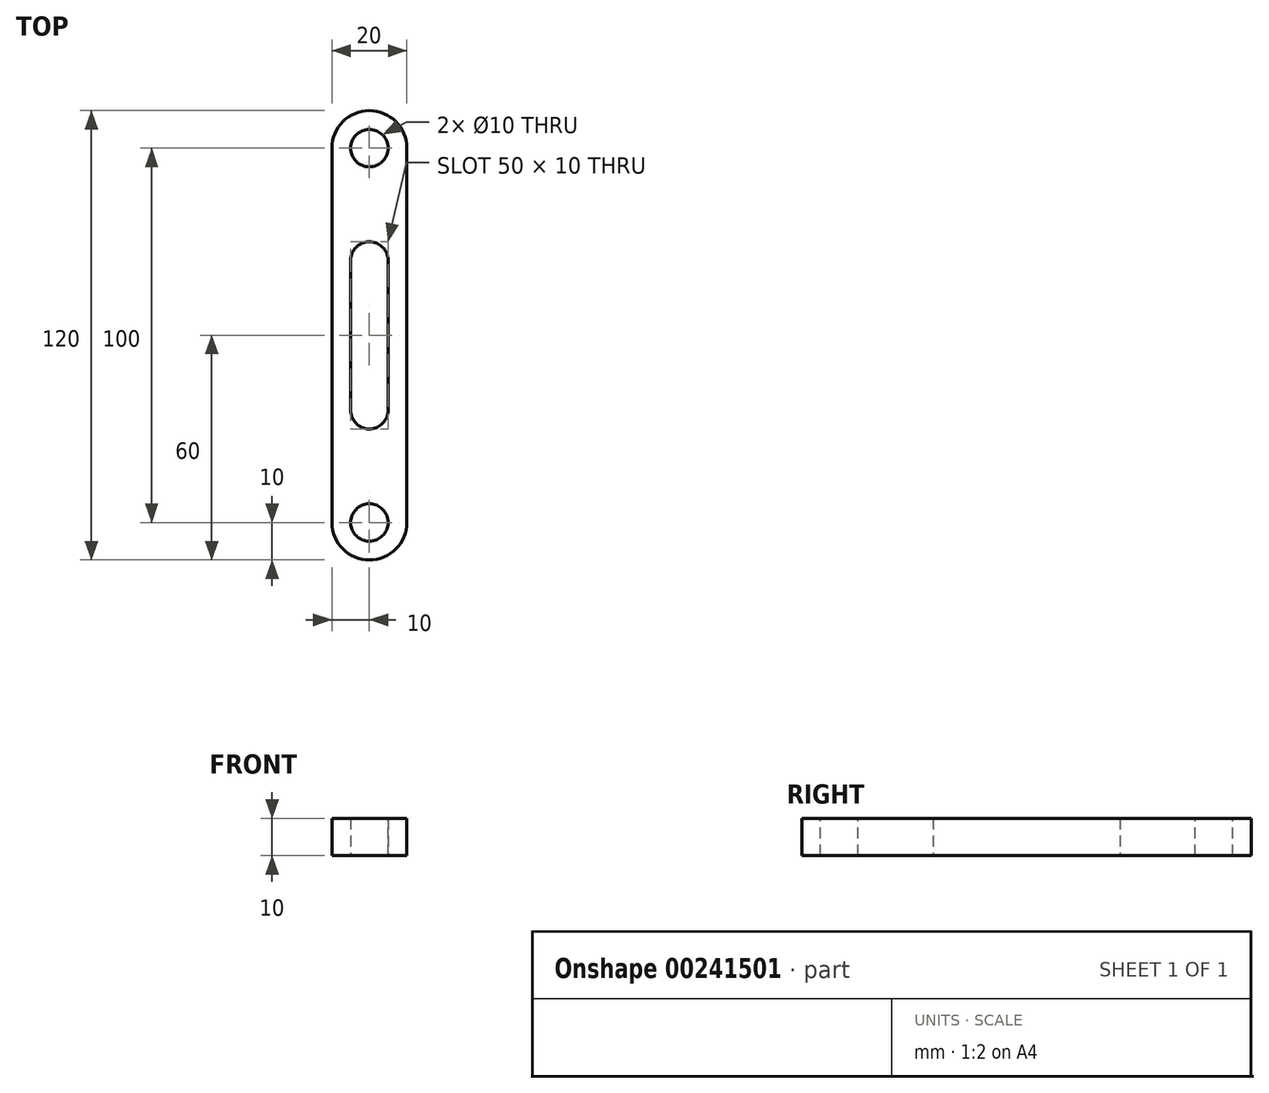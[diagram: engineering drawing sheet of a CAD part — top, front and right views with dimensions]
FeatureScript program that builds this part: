
annotation { "Feature Type Name" : "Feature", "Feature Type Description" : "" }
export const myFeature = defineFeature(function(context is Context, id is Id, definition is map)
    precondition{}
    {
        {
            var Q0;
            Q0=qCreatedBy(makeId("Top.planeOp"),FACE);
            var sketch = newSketch(context, id + "F0", { "sketchPlane" : qUnion([Q0])});
            skArc(sketch, "E0", {"start": v(10, 0) * mm, "mid": v(0, 10) * mm, "end": v(-10, 0) * mm});
            skLineSegment(sketch, "E1", {"start": v(-10, 0) * mm, "end": v(-10, -100) * mm});
            skLineSegment(sketch, "E2", {"start": v(10, 0) * mm, "end": v(10, -100) * mm});
            skArc(sketch, "E3", {"start": v(-10, -100) * mm, "mid": v(0, -110) * mm, "end": v(10, -100) * mm});
            skLineSegment(sketch, "E4.0", {"start": v(5, -30) * mm, "end": v(5, -70) * mm});
            skLineSegment(sketch, "E5.0", {"start": v(-5, -30) * mm, "end": v(-5, -70) * mm});
            skArc(sketch, "E6", {"start": v(5, -30) * mm, "mid": v(0, -25) * mm, "end": v(-5, -30) * mm});
            skArc(sketch, "E7", {"start": v(-5, -70) * mm, "mid": v(0, -75) * mm, "end": v(5, -70) * mm});
            skSolve(sketch);
        }
        {
            var Q0;
            Q0 = qSketchRegion(id + "F0", true);
            extrude(context, id + "F1", {"entities" : qUnion([Q0]), "depth" : 10 * mm});
        }
        {
            var Q0;
            Q0=makeQuery(id+"F1.opExtrude","CAP_FACE",FACE,{"disambiguationData":[OSD([sQuery(id+"F0.wireOp",EDGE,"E0"),sQuery(id+"F0.wireOp",EDGE,"E1"),sQuery(id+"F0.wireOp",EDGE,"E2"),sQuery(id+"F0.wireOp",EDGE,"E3"),sQuery(id+"F0.wireOp",EDGE,"E4.0"),sQuery(id+"F0.wireOp",EDGE,"E5.0"),sQuery(id+"F0.wireOp",EDGE,"E6"),sQuery(id+"F0.wireOp",EDGE,"E7")])],"isStart":false});
            var sketch = newSketch(context, id + "F2", { "sketchPlane" : qUnion([Q0])});
            skPoint(sketch, "E8", {"position": v(0, 0) * mm});
            skPoint(sketch, "E9", {"position": v(0, -100) * mm});
            skSolve(sketch);
        }
        {
            var Q0;
            Q0=sQuery(id+"F2.wireOp",VERTEX,"E8");
            var Q1;
            Q1=sQuery(id+"F2.wireOp",VERTEX,"E9");
            var Q2;
            Q2=makeQuery(id+"F1.opExtrude","SWEPT_BODY",BODY,{"disambiguationData":[OSD([sQuery(id+"F0.wireOp",EDGE,"E0"),sQuery(id+"F0.wireOp",EDGE,"E1"),sQuery(id+"F0.wireOp",EDGE,"E2"),sQuery(id+"F0.wireOp",EDGE,"E3"),sQuery(id+"F0.wireOp",EDGE,"E4.0"),sQuery(id+"F0.wireOp",EDGE,"E5.0"),sQuery(id+"F0.wireOp",EDGE,"E6"),sQuery(id+"F0.wireOp",EDGE,"E7")])]});
            hole(context, id + "F3", {"style" : HoleStyle.SIMPLE, "endStyle" : HoleEndStyle.THROUGH, "holeDiameter" : 10 * mm, "startFromSketch" : true, "locations" : qUnion([Q0, Q1]), "scope" : qUnion([Q2]), "isTappedThrough" : true});
        }
    });
